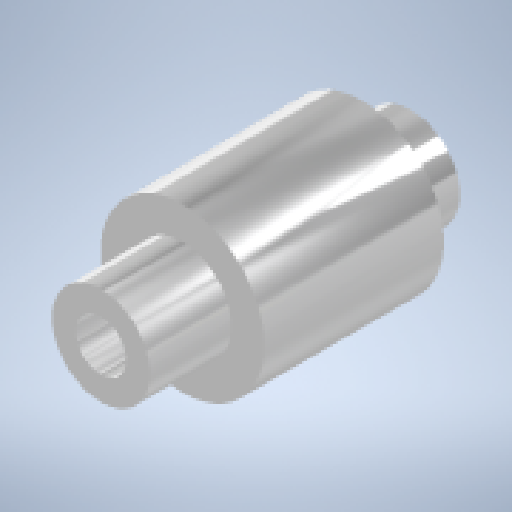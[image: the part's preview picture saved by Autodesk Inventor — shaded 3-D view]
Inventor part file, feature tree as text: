
AUTODESK INVENTOR PART (.ipt)
format: ipt  version: 2024 (Build 280153000, 153)  size: 158,208 bytes
history: native  units: mm
features: sketch x2, other x1, revolve x1, hole x1
ambient origin geometry x8: Origin, YZ Plane, XZ Plane, XY Plane, X Axis, Y Axis, Z Axis, Center Point
bodies: Body1 (feature_tree)
feature tree (5):
  other  "ソリッド1"
  revolve  "回転1"
  hole  "穴1"  [1 undecoded]
  sketch  "スケッチ1"
  sketch  "スケッチ2"
note: 1 required parameter value undecoded (feature->parameter linkage not recoverable at this tier; creation-order binding heuristic only, values carry confidence <= 0.55)
